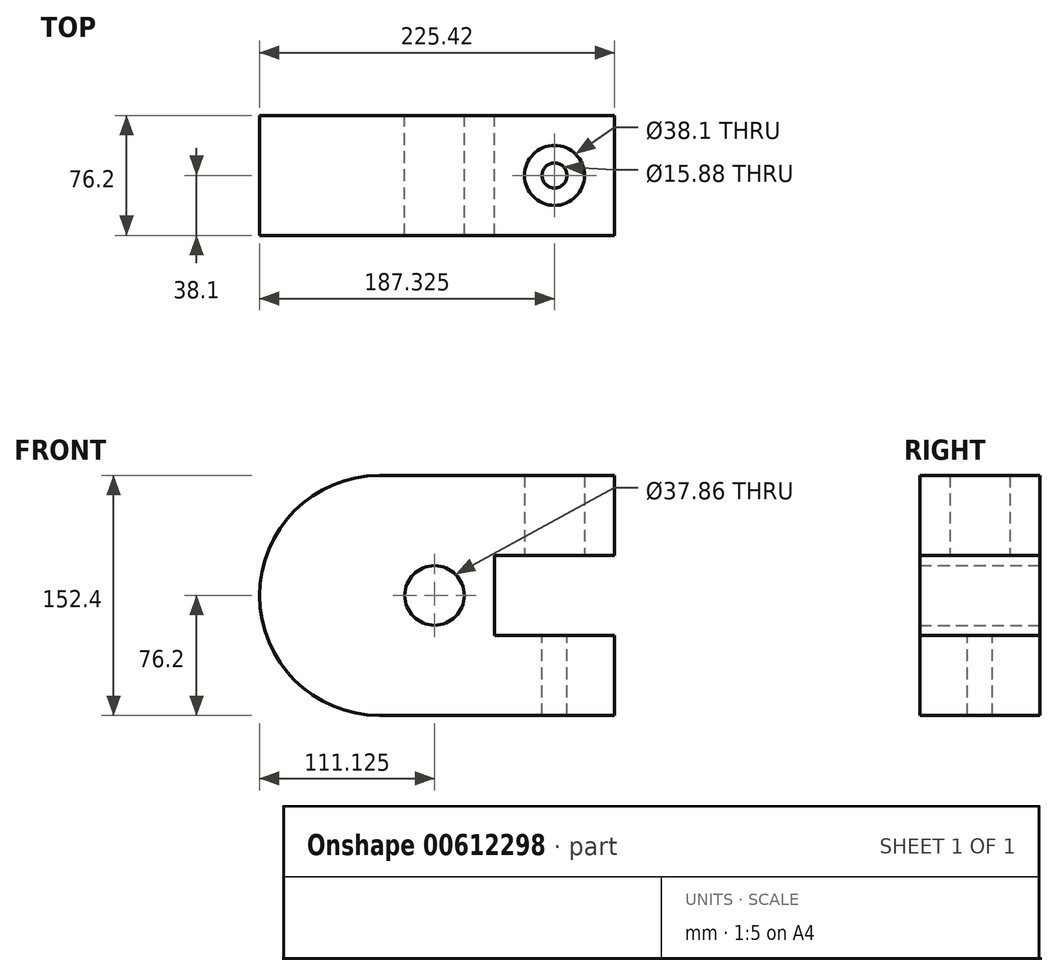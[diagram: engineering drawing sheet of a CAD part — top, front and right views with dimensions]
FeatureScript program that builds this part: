
annotation { "Feature Type Name" : "Feature", "Feature Type Description" : "" }
export const myFeature = defineFeature(function(context is Context, id is Id, definition is map)
    precondition{}
    {
        {
            var Q0;
            Q0=qCreatedBy(makeId("Front.planeOp"),FACE);
            var sketch = newSketch(context, id + "F0", { "sketchPlane" : qUnion([Q0])});
            skLineSegment(sketch, "E0", {"start": v(0, 0) * mm, "end": v(149.22, 0) * mm});
            skLineSegment(sketch, "E1", {"start": v(0, 0) * mm, "end": v(0, -152.4) * mm});
            skLineSegment(sketch, "E2", {"start": v(0, -152.4) * mm, "end": v(149.23, -152.4) * mm});
            skLineSegment(sketch, "E3", {"start": v(149.23, -152.4) * mm, "end": v(149.23, -101.6) * mm});
            skLineSegment(sketch, "E4", {"start": v(149.22, -101.6) * mm, "end": v(73.02, -101.6) * mm});
            skLineSegment(sketch, "E5", {"start": v(73.03, -101.6) * mm, "end": v(73.03, -50.8) * mm});
            skLineSegment(sketch, "E6", {"start": v(73.02, -50.8) * mm, "end": v(149.22, -50.8) * mm});
            skLineSegment(sketch, "E7", {"start": v(149.22, -50.8) * mm, "end": v(149.22, 0) * mm});
            skArc(sketch, "E8", {"start": v(0, 0) * mm, "mid": v(-76.2, -76.2) * mm, "end": v(0, -152.4) * mm});
            skCircle(sketch, "E9", {"center": v(34.93, -76.2) * mm, "radius": 18.93 * mm});
            skSolve(sketch);
        }
        {
            var Q0;
            Q0=makeQuery(id+"F0.imprint","IMPRINT",FACE,{"disambiguationData":[TD([[makeQuery(id+"F0.imprint","IMPRINT",EDGE,{"derivedFrom":sQuery(id+"F0.wireOp",EDGE,"E1")}),-1.0]])]});
            var Q1;
            Q1=makeQuery(id+"F0.imprint","IMPRINT",FACE,{"disambiguationData":[TD([[makeQuery(id+"F0.imprint","IMPRINT",EDGE,{"derivedFrom":sQuery(id+"F0.wireOp",EDGE,"E0")}),-1.0]])]});
            extrude(context, id + "F1", {"entities" : qUnion([Q0, Q1]), "depth" : 76.2 * mm, "offsetDistance" : 25.4 * mm});
        }
        {
            var Q0;
            Q0=makeQuery(id+"F1.opExtrude","SWEPT_FACE",FACE,{"disambiguationData":[OSD([sQuery(id+"F0.wireOp",EDGE,"E4")])]});
            var sketch = newSketch(context, id + "F2", { "sketchPlane" : qUnion([Q0])});
            skCircle(sketch, "E10", {"center": v(111.13, -38.1) * mm, "radius": 7.94 * mm});
            skSolve(sketch);
        }
        {
            var Q0;
            Q0=makeQuery(id+"F1.opExtrude","SWEPT_FACE",FACE,{"disambiguationData":[OSD([sQuery(id+"F0.wireOp",EDGE,"E6")])]});
            var sketch = newSketch(context, id + "F3", { "sketchPlane" : qUnion([Q0])});
            skCircle(sketch, "E11", {"center": v(111.12, 38.1) * mm, "radius": 19.05 * mm});
            skSolve(sketch);
        }
        {
            var Q0;
            Q0=sQuery(id+"F3.wireOp",VERTEX,"E11.center");
            var Q1;
            Q1=makeQuery(id+"F1.opExtrude","SWEPT_BODY",BODY,{"disambiguationData":[OSD([sQuery(id+"F0.wireOp",EDGE,"E0"),sQuery(id+"F0.wireOp",EDGE,"E2"),sQuery(id+"F0.wireOp",EDGE,"E3"),sQuery(id+"F0.wireOp",EDGE,"E4"),sQuery(id+"F0.wireOp",EDGE,"E5"),sQuery(id+"F0.wireOp",EDGE,"E6"),sQuery(id+"F0.wireOp",EDGE,"E7"),sQuery(id+"F0.wireOp",EDGE,"E8"),sQuery(id+"F0.wireOp",EDGE,"E9")])]});
            hole(context, id + "F4", {"style" : HoleStyle.SIMPLE, "endStyle" : HoleEndStyle.BLIND, "holeDiameter" : 38.1 * mm, "majorDiameter" : 6.35 * mm, "holeDepth" : 50.8 * mm, "isTappedThrough" : true, "tappedDepth" : 12.7 * mm, "tapClearance" : 3, "locations" : qUnion([Q0]), "scope" : qUnion([Q1])});
        }
        {
            var Q0;
            Q0=sQuery(id+"F2.wireOp",VERTEX,"E10.center");
            var Q1;
            Q1=makeQuery(id+"F1.opExtrude","SWEPT_BODY",BODY,{"disambiguationData":[OSD([sQuery(id+"F0.wireOp",EDGE,"E0"),sQuery(id+"F0.wireOp",EDGE,"E2"),sQuery(id+"F0.wireOp",EDGE,"E3"),sQuery(id+"F0.wireOp",EDGE,"E4"),sQuery(id+"F0.wireOp",EDGE,"E5"),sQuery(id+"F0.wireOp",EDGE,"E6"),sQuery(id+"F0.wireOp",EDGE,"E7"),sQuery(id+"F0.wireOp",EDGE,"E8"),sQuery(id+"F0.wireOp",EDGE,"E9")])]});
            hole(context, id + "F5", {"style" : HoleStyle.SIMPLE, "endStyle" : HoleEndStyle.BLIND, "holeDiameter" : 15.88 * mm, "majorDiameter" : 6.35 * mm, "holeDepth" : 50.8 * mm, "isTappedThrough" : true, "tappedDepth" : 12.7 * mm, "tapClearance" : 3, "locations" : qUnion([Q0]), "scope" : qUnion([Q1])});
        }
    });
